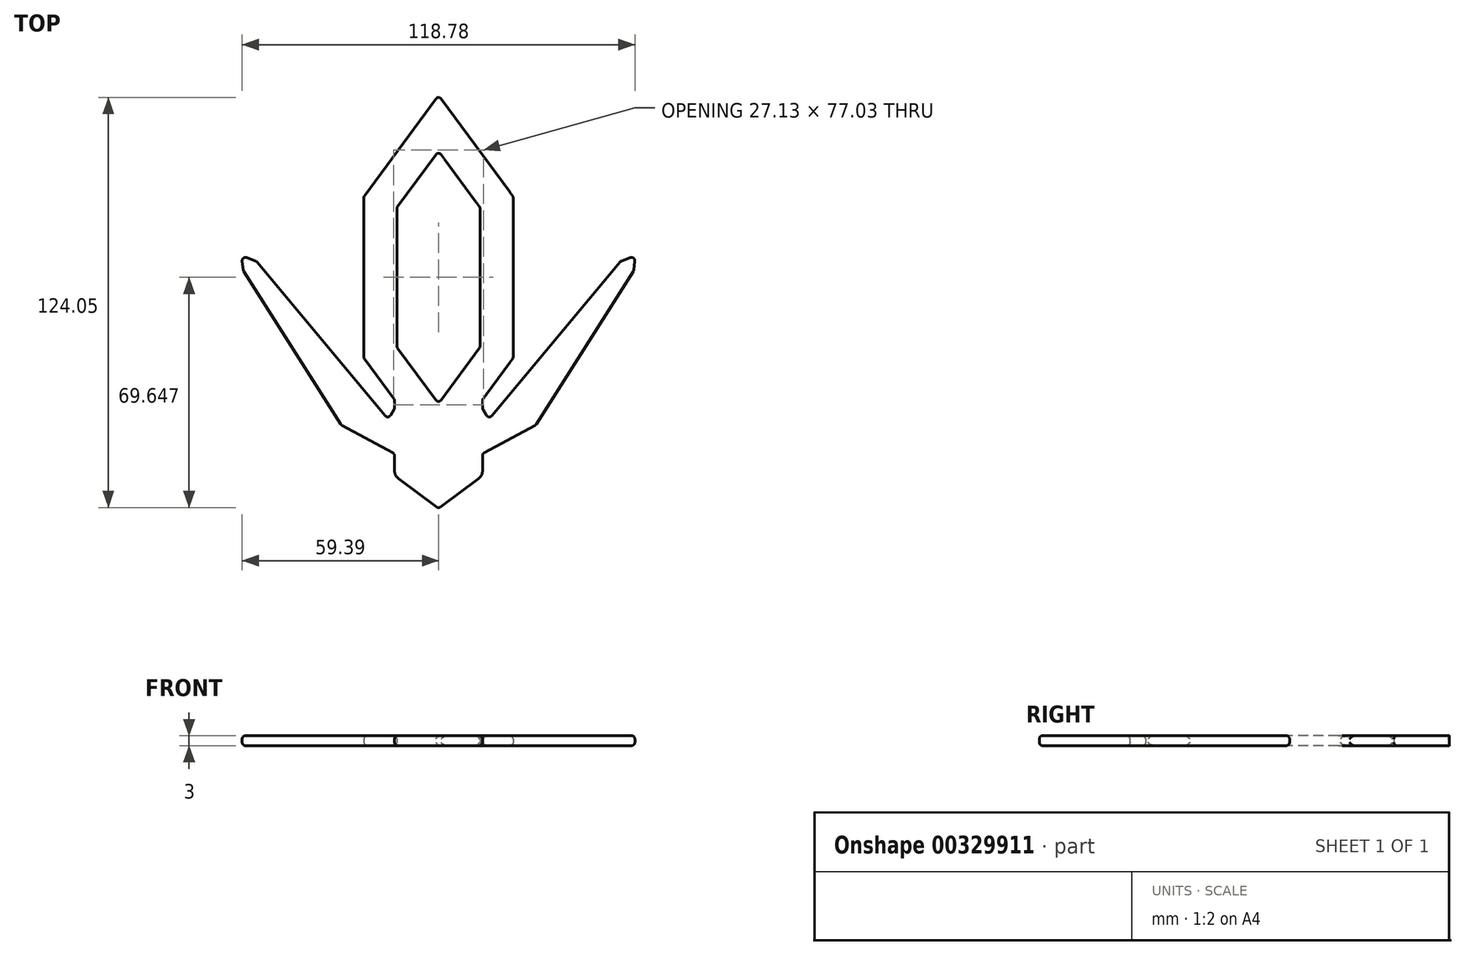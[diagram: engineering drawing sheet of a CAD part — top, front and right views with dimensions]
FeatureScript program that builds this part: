
annotation { "Feature Type Name" : "Feature", "Feature Type Description" : "" }
export const myFeature = defineFeature(function(context is Context, id is Id, definition is map)
    precondition{}
    {
        {
            var Q0;
            Q0=qCreatedBy(makeId("Top.planeOp"),FACE);
            var sketch = newSketch(context, id + "F0", { "sketchPlane" : qUnion([Q0])});
            skLineSegment(sketch, "E0", {"start": v(0, 55.08) * mm, "end": v(22.57, 24.43) * mm});
            skLineSegment(sketch, "E1", {"start": v(22.57, 24.43) * mm, "end": v(22.57, 0) * mm});
            skLineSegment(sketch, "E2.0", {"start": v(12.57, 21.15) * mm, "end": v(12.57, 0) * mm});
            skLineSegment(sketch, "E2.1", {"start": v(0, 38.21) * mm, "end": v(12.57, 21.15) * mm});
            skLineSegment(sketch, "E3.MirrorCS", {"start": v(-22.57, 24.43) * mm, "end": v(-22.57, 0) * mm});
            skLineSegment(sketch, "E4.MirrorCS", {"start": v(-12.57, 21.15) * mm, "end": v(-12.57, 0) * mm});
            skLineSegment(sketch, "E5.MirrorCS", {"start": v(0, 38.21) * mm, "end": v(-12.57, 21.15) * mm});
            skLineSegment(sketch, "E6.MirrorCS", {"start": v(0, 55.08) * mm, "end": v(-22.57, 24.43) * mm});
            skLineSegment(sketch, "E7.MirrorCS", {"start": v(-4.03, 49.61) * mm, "end": v(-22.57, 24.43) * mm});
            skLineSegment(sketch, "E8.MirrorCS", {"start": v(-22.57, 23.45) * mm, "end": v(-22.57, 0) * mm});
            skLineSegment(sketch, "E9.MirrorCS", {"start": v(12.57, 20.16) * mm, "end": v(12.57, 0) * mm});
            skLineSegment(sketch, "E10.MirrorCS", {"start": v(-12.57, 20.16) * mm, "end": v(-12.57, 0) * mm});
            skLineSegment(sketch, "E11.MirrorCS", {"start": v(-2.42, 34.93) * mm, "end": v(-11.98, 21.94) * mm});
            skLineSegment(sketch, "E12.MirrorCS", {"start": v(4.03, 49.61) * mm, "end": v(21.98, 25.23) * mm});
            skLineSegment(sketch, "E13.MirrorCS", {"start": v(0, 55.08) * mm, "end": v(-21.98, 25.23) * mm});
            skLineSegment(sketch, "E14.MirrorCS", {"start": v(22.57, 23.45) * mm, "end": v(22.57, 0) * mm});
            skLineSegment(sketch, "E15.MirrorCS", {"start": v(2.42, 34.93) * mm, "end": v(11.98, 21.94) * mm});
            skPoint(sketch, "E16.visualSharp", {"position": v(0, 55.08) * mm});
            skArc(sketch, "E16.filletArc", {"start": v(4.03, 49.61) * mm, "mid": v(0, 51.65) * mm, "end": v(-4.03, 49.61) * mm});
            skPoint(sketch, "E17.visualSharp", {"position": v(0, 38.21) * mm});
            skArc(sketch, "E17.filletArc", {"start": v(2.42, 34.93) * mm, "mid": v(0, 36.15) * mm, "end": v(-2.42, 34.93) * mm});
            skPoint(sketch, "E18.visualSharp", {"position": v(12.57, 21.15) * mm});
            skArc(sketch, "E18.filletArc", {"start": v(12.57, 20.16) * mm, "mid": v(12.42, 21.1) * mm, "end": v(11.98, 21.94) * mm});
            skPoint(sketch, "E19.visualSharp", {"position": v(-12.57, 21.15) * mm});
            skArc(sketch, "E19.filletArc", {"start": v(-11.98, 21.94) * mm, "mid": v(-12.42, 21.1) * mm, "end": v(-12.57, 20.16) * mm});
            skPoint(sketch, "E20.visualSharp", {"position": v(-22.57, 24.43) * mm});
            skArc(sketch, "E20.filletArc", {"start": v(-21.98, 25.23) * mm, "mid": v(-22.42, 24.39) * mm, "end": v(-22.57, 23.45) * mm});
            skPoint(sketch, "E21.visualSharp", {"position": v(22.57, 24.43) * mm});
            skArc(sketch, "E21.filletArc", {"start": v(22.57, 23.45) * mm, "mid": v(22.42, 24.39) * mm, "end": v(21.98, 25.23) * mm});
            skArc(sketch, "E22.MirrorCS", {"start": v(2.42, -34.93) * mm, "mid": v(0, -36.15) * mm, "end": v(-2.42, -34.93) * mm});
            skArc(sketch, "E23.MirrorCS", {"start": v(-11.98, -21.94) * mm, "mid": v(-12.42, -21.1) * mm, "end": v(-12.57, -20.16) * mm});
            skArc(sketch, "E24.MirrorCS", {"start": v(12.57, -20.16) * mm, "mid": v(12.42, -21.1) * mm, "end": v(11.98, -21.94) * mm});
            skArc(sketch, "E25.MirrorCS", {"start": v(-21.98, -25.23) * mm, "mid": v(-22.42, -24.39) * mm, "end": v(-22.57, -23.45) * mm});
            skArc(sketch, "E26.MirrorCS", {"start": v(22.57, -23.45) * mm, "mid": v(22.42, -24.39) * mm, "end": v(21.98, -25.23) * mm});
            skLineSegment(sketch, "E27.MirrorCS", {"start": v(12.57, -21.15) * mm, "end": v(12.57, 0) * mm});
            skLineSegment(sketch, "E28.MirrorCS", {"start": v(22.57, -24.43) * mm, "end": v(22.57, 0) * mm});
            skLineSegment(sketch, "E29.MirrorCS", {"start": v(-12.57, -21.15) * mm, "end": v(-12.57, 0) * mm});
            skLineSegment(sketch, "E30.MirrorCS", {"start": v(0, -38.21) * mm, "end": v(12.57, -21.15) * mm});
            skLineSegment(sketch, "E31.MirrorCS", {"start": v(-22.57, -24.43) * mm, "end": v(-22.57, 0) * mm});
            skLineSegment(sketch, "E32.MirrorCS", {"start": v(0, -38.21) * mm, "end": v(-12.57, -21.15) * mm});
            skLineSegment(sketch, "E33.MirrorCS", {"start": v(0, -55.08) * mm, "end": v(-22.57, -24.43) * mm});
            skLineSegment(sketch, "E34.MirrorCS", {"start": v(0, -55.08) * mm, "end": v(22.57, -24.43) * mm});
            skLineSegment(sketch, "E35.MirrorCS", {"start": v(-4.03, -49.61) * mm, "end": v(-22.57, -24.43) * mm});
            skPoint(sketch, "E36.MirrorP", {"position": v(0, -38.21) * mm});
            skLineSegment(sketch, "E37.MirrorCS", {"start": v(22.57, -23.45) * mm, "end": v(22.57, 0) * mm});
            skLineSegment(sketch, "E38.MirrorCS", {"start": v(4.03, -49.61) * mm, "end": v(21.98, -25.23) * mm});
            skLineSegment(sketch, "E39.MirrorCS", {"start": v(-2.42, -34.93) * mm, "end": v(-11.98, -21.94) * mm});
            skPoint(sketch, "E40.MirrorP", {"position": v(-22.57, -24.43) * mm});
            skPoint(sketch, "E41.MirrorP", {"position": v(22.57, -24.43) * mm});
            skLineSegment(sketch, "E42.MirrorCS", {"start": v(-22.57, -23.45) * mm, "end": v(-22.57, 0) * mm});
            skPoint(sketch, "E43.MirrorP", {"position": v(-12.57, -21.15) * mm});
            skPoint(sketch, "E44.MirrorP", {"position": v(12.57, -21.15) * mm});
            skLineSegment(sketch, "E45.MirrorCS", {"start": v(12.57, -20.16) * mm, "end": v(12.57, 0) * mm});
            skLineSegment(sketch, "E46.MirrorCS", {"start": v(0, -55.08) * mm, "end": v(-21.98, -25.23) * mm});
            skLineSegment(sketch, "E47.MirrorCS", {"start": v(-12.57, -20.16) * mm, "end": v(-12.57, 0) * mm});
            skLineSegment(sketch, "E48.MirrorCS", {"start": v(2.42, -34.93) * mm, "end": v(11.98, -21.94) * mm});
            skPoint(sketch, "E49.MirrorP", {"position": v(0, -55.08) * mm});
            skLineSegment(sketch, "E50", {"start": v(-13.3, -37.02) * mm, "end": v(-13.3, -58.54) * mm});
            skLineSegment(sketch, "E51", {"start": v(-12.08, -60.95) * mm, "end": v(0, -69.9) * mm});
            skPoint(sketch, "E52.visualSharp", {"position": v(-13.3, -60.05) * mm});
            skArc(sketch, "E52.filletArc", {"start": v(-13.3, -58.54) * mm, "mid": v(-12.98, -59.88) * mm, "end": v(-12.08, -60.95) * mm});
            skArc(sketch, "E53.MirrorCS", {"start": v(13.3, -58.54) * mm, "mid": v(12.98, -59.88) * mm, "end": v(12.08, -60.95) * mm});
            skLineSegment(sketch, "E54.MirrorCS", {"start": v(13.3, -37.02) * mm, "end": v(13.3, -58.54) * mm});
            skLineSegment(sketch, "E55.MirrorCS", {"start": v(12.08, -60.95) * mm, "end": v(0, -69.9) * mm});
            skPoint(sketch, "E56.MirrorP", {"position": v(13.3, -60.05) * mm});
            skPoint(sketch, "E57.endSnap0", {"position": v(-13.3, -47.78) * mm});
            skLineSegment(sketch, "E58", {"start": v(-13.3, -39.76) * mm, "end": v(-15.24, -42.93) * mm});
            skPoint(sketch, "E58.startSnap0", {"position": v(-11.28, -39.76) * mm});
            skLineSegment(sketch, "E59", {"start": v(-15.24, -42.93) * mm, "end": v(-55.04, 4.83) * mm});
            skLineSegment(sketch, "E60", {"start": v(-55.04, 4.83) * mm, "end": v(-59.6, 6.54) * mm});
            skLineSegment(sketch, "E61", {"start": v(-59.6, 6.54) * mm, "end": v(-59.02, 1.99) * mm});
            skLineSegment(sketch, "E62", {"start": v(-59.02, 1.99) * mm, "end": v(-29.45, -44.64) * mm});
            skLineSegment(sketch, "E63", {"start": v(-29.45, -44.64) * mm, "end": v(-13.3, -53.38) * mm});
            skLineSegment(sketch, "E64.MirrorCS", {"start": v(13.3, -39.76) * mm, "end": v(15.24, -42.93) * mm});
            skLineSegment(sketch, "E65.MirrorCS", {"start": v(29.45, -44.64) * mm, "end": v(13.3, -53.38) * mm});
            skLineSegment(sketch, "E66.MirrorCS", {"start": v(15.24, -42.93) * mm, "end": v(55.04, 4.83) * mm});
            skLineSegment(sketch, "E67.MirrorCS", {"start": v(55.04, 4.83) * mm, "end": v(59.6, 6.54) * mm});
            skLineSegment(sketch, "E68.MirrorCS", {"start": v(59.02, 1.99) * mm, "end": v(29.45, -44.64) * mm});
            skLineSegment(sketch, "E69.MirrorCS", {"start": v(59.6, 6.54) * mm, "end": v(59.02, 1.99) * mm});
            skSolve(sketch);
        }
        {
            var Q0;
            Q0 = qSketchRegion(id + "F0", true);
            extrude(context, id + "F1", {"entities" : qUnion([Q0]), "depth" : 3 * mm});
        }
        {
            var Q0;
            Q0=makeQuery(id+"F1.opExtrude","CAP_EDGE",EDGE,{"disambiguationData":[OSD([sQuery(id+"F0.wireOp",EDGE,"E33.MirrorCS"),sQuery(id+"F0.wireOp",EDGE,"E46.MirrorCS")])],"isStart":true});
            var Q1;
            Q1=makeQuery(id+"F1.opExtrude","CAP_EDGE",EDGE,{"disambiguationData":[OSD([sQuery(id+"F0.wireOp",EDGE,"E33.MirrorCS"),sQuery(id+"F0.wireOp",EDGE,"E46.MirrorCS")])],"isStart":false});
            var Q2;
            Q2=makeQuery(id+"F1.opExtrude","CAP_EDGE",EDGE,{"disambiguationData":[OSD([sQuery(id+"F0.wireOp",EDGE,"E4.MirrorCS"),sQuery(id+"F0.wireOp",EDGE,"E29.MirrorCS"),sQuery(id+"F0.wireOp",EDGE,"E47.MirrorCS")])],"isStart":false});
            var Q3;
            Q3=makeQuery(id+"F1.opExtrude","CAP_EDGE",EDGE,{"disambiguationData":[OSD([sQuery(id+"F0.wireOp",EDGE,"E3.MirrorCS"),sQuery(id+"F0.wireOp",EDGE,"E31.MirrorCS"),sQuery(id+"F0.wireOp",EDGE,"E42.MirrorCS")])],"isStart":true});
            var Q4;
            Q4=makeQuery(id+"F1.opExtrude","CAP_EDGE",EDGE,{"disambiguationData":[OSD([sQuery(id+"F0.wireOp",EDGE,"E3.MirrorCS"),sQuery(id+"F0.wireOp",EDGE,"E31.MirrorCS"),sQuery(id+"F0.wireOp",EDGE,"E42.MirrorCS")])],"isStart":false});
            var Q5;
            {var subQ0=sQuery(id+"F0.wireOp",EDGE,"E50");Q5=makeQuery(id+"F1.opExtrude","CAP_EDGE",EDGE,{"disambiguationData":[OSD([subQ0]),TDD([makeQuery(id+"F0.imprint","IMPRINT",EDGE,{"disambiguationData":[TD([[makeQuery(id+"F0.imprint","INTERSECT",VERTEX,{"derivedFrom":[sQuery(id+"F0.wireOp",EDGE,"E46.MirrorCS"),subQ0]}),-1.0]])],"derivedFrom":subQ0})])],"isStart":true});}
            var Q6;
            Q6=makeQuery(id+"F1.opExtrude","SWEPT_EDGE",EDGE,{"disambiguationData":[OSD([sQuery(id+"F0.wireOp",EDGE,"E32.MirrorCS"),sQuery(id+"F0.wireOp",EDGE,"E29.MirrorCS")])]});
            var Q7;
            {var subQ0=sQuery(id+"F0.wireOp",EDGE,"E50");Q7=makeQuery(id+"F1.opExtrude","CAP_EDGE",EDGE,{"disambiguationData":[OSD([subQ0]),TDD([makeQuery(id+"F0.imprint","IMPRINT",EDGE,{"disambiguationData":[TD([[makeQuery(id+"F0.imprint","INTERSECT",VERTEX,{"derivedFrom":[sQuery(id+"F0.wireOp",EDGE,"E46.MirrorCS"),subQ0]}),-1.0]])],"derivedFrom":subQ0})])],"isStart":false});}
            var Q8;
            Q8=makeQuery(id+"F1.opExtrude","CAP_EDGE",EDGE,{"disambiguationData":[OSD([sQuery(id+"F0.wireOp",EDGE,"E4.MirrorCS"),sQuery(id+"F0.wireOp",EDGE,"E29.MirrorCS"),sQuery(id+"F0.wireOp",EDGE,"E47.MirrorCS")])],"isStart":true});
            var Q9;
            Q9=makeQuery(id+"F1.opExtrude","SWEPT_EDGE",EDGE,{"disambiguationData":[OSD([sQuery(id+"F0.wireOp",EDGE,"E46.MirrorCS"),sQuery(id+"F0.wireOp",EDGE,"E50")])]});
            var Q10;
            Q10=makeQuery(id+"F1.opExtrude","SWEPT_EDGE",EDGE,{"disambiguationData":[OSD([sQuery(id+"F0.wireOp",EDGE,"E31.MirrorCS"),sQuery(id+"F0.wireOp",EDGE,"E33.MirrorCS")])]});
            var Q11;
            Q11=makeQuery(id+"F1.opExtrude","SWEPT_EDGE",EDGE,{"disambiguationData":[OSD([sQuery(id+"F0.wireOp",EDGE,"E3.MirrorCS"),sQuery(id+"F0.wireOp",EDGE,"E6.MirrorCS")])]});
            var Q12;
            Q12=makeQuery(id+"F1.opExtrude","SWEPT_EDGE",EDGE,{"disambiguationData":[OSD([sQuery(id+"F0.wireOp",EDGE,"E4.MirrorCS"),sQuery(id+"F0.wireOp",EDGE,"E5.MirrorCS")])]});
            var Q13;
            Q13=makeQuery(id+"F1.opExtrude","SWEPT_EDGE",EDGE,{"disambiguationData":[OSD([sQuery(id+"F0.wireOp",EDGE,"E50"),sQuery(id+"F0.wireOp",EDGE,"E52.filletArc")])]});
            var Q14;
            Q14=makeQuery(id+"F1.opExtrude","SWEPT_EDGE",EDGE,{"disambiguationData":[OSD([sQuery(id+"F0.wireOp",EDGE,"E50"),sQuery(id+"F0.wireOp",EDGE,"E58")])]});
            var Q15;
            Q15=makeQuery(id+"F1.opExtrude","SWEPT_EDGE",EDGE,{"disambiguationData":[OSD([sQuery(id+"F0.wireOp",EDGE,"E50"),sQuery(id+"F0.wireOp",EDGE,"E63")])]});
            var Q16;
            Q16=makeQuery(id+"F1.opExtrude","CAP_EDGE",EDGE,{"disambiguationData":[OSD([sQuery(id+"F0.wireOp",EDGE,"E30.MirrorCS"),sQuery(id+"F0.wireOp",EDGE,"E48.MirrorCS")])],"isStart":false});
            var Q17;
            Q17=makeQuery(id+"F1.opExtrude","CAP_EDGE",EDGE,{"disambiguationData":[OSD([sQuery(id+"F0.wireOp",EDGE,"E32.MirrorCS"),sQuery(id+"F0.wireOp",EDGE,"E39.MirrorCS")])],"isStart":false});
            var Q18;
            Q18=makeQuery(id+"F1.opExtrude","CAP_EDGE",EDGE,{"disambiguationData":[OSD([sQuery(id+"F0.wireOp",EDGE,"E2.1")])],"isStart":false});
            var Q19;
            Q19=makeQuery(id+"F1.opExtrude","CAP_EDGE",EDGE,{"disambiguationData":[OSD([sQuery(id+"F0.wireOp",EDGE,"E1"),sQuery(id+"F0.wireOp",EDGE,"E28.MirrorCS"),sQuery(id+"F0.wireOp",EDGE,"E37.MirrorCS")])],"isStart":false});
            var Q20;
            Q20=makeQuery(id+"F1.opExtrude","CAP_EDGE",EDGE,{"disambiguationData":[OSD([sQuery(id+"F0.wireOp",EDGE,"E32.MirrorCS"),sQuery(id+"F0.wireOp",EDGE,"E39.MirrorCS")])],"isStart":true});
            var Q21;
            Q21=makeQuery(id+"F1.opExtrude","CAP_EDGE",EDGE,{"disambiguationData":[OSD([sQuery(id+"F0.wireOp",EDGE,"E5.MirrorCS")])],"isStart":false});
            var Q22;
            Q22=makeQuery(id+"F1.opExtrude","CAP_EDGE",EDGE,{"disambiguationData":[OSD([sQuery(id+"F0.wireOp",EDGE,"E34.MirrorCS"),sQuery(id+"F0.wireOp",EDGE,"E38.MirrorCS")])],"isStart":false});
            var Q23;
            Q23=makeQuery(id+"F1.opExtrude","CAP_EDGE",EDGE,{"disambiguationData":[OSD([sQuery(id+"F0.wireOp",EDGE,"E0")])],"isStart":false});
            var Q24;
            Q24=makeQuery(id+"F1.opExtrude","CAP_EDGE",EDGE,{"disambiguationData":[OSD([sQuery(id+"F0.wireOp",EDGE,"E0")])],"isStart":true});
            var Q25;
            Q25=makeQuery(id+"F1.opExtrude","CAP_EDGE",EDGE,{"disambiguationData":[OSD([sQuery(id+"F0.wireOp",EDGE,"E5.MirrorCS")])],"isStart":true});
            var Q26;
            Q26=makeQuery(id+"F1.opExtrude","CAP_EDGE",EDGE,{"disambiguationData":[OSD([sQuery(id+"F0.wireOp",EDGE,"E6.MirrorCS")])],"isStart":false});
            var Q27;
            Q27=makeQuery(id+"F1.opExtrude","CAP_EDGE",EDGE,{"disambiguationData":[OSD([sQuery(id+"F0.wireOp",EDGE,"E55.MirrorCS")])],"isStart":false});
            var Q28;
            Q28=makeQuery(id+"F1.opExtrude","CAP_EDGE",EDGE,{"disambiguationData":[OSD([sQuery(id+"F0.wireOp",EDGE,"E55.MirrorCS")])],"isStart":true});
            var Q29;
            Q29=makeQuery(id+"F1.opExtrude","CAP_EDGE",EDGE,{"disambiguationData":[OSD([sQuery(id+"F0.wireOp",EDGE,"E52.filletArc")])],"isStart":false});
            var Q30;
            Q30=makeQuery(id+"F1.opExtrude","CAP_EDGE",EDGE,{"disambiguationData":[OSD([sQuery(id+"F0.wireOp",EDGE,"E2.0"),sQuery(id+"F0.wireOp",EDGE,"E27.MirrorCS"),sQuery(id+"F0.wireOp",EDGE,"E45.MirrorCS")])],"isStart":true});
            var Q31;
            Q31=makeQuery(id+"F1.opExtrude","CAP_EDGE",EDGE,{"disambiguationData":[OSD([sQuery(id+"F0.wireOp",EDGE,"E2.0"),sQuery(id+"F0.wireOp",EDGE,"E27.MirrorCS"),sQuery(id+"F0.wireOp",EDGE,"E45.MirrorCS")])],"isStart":false});
            var Q32;
            Q32=makeQuery(id+"F1.opExtrude","CAP_EDGE",EDGE,{"disambiguationData":[OSD([sQuery(id+"F0.wireOp",EDGE,"E1"),sQuery(id+"F0.wireOp",EDGE,"E28.MirrorCS"),sQuery(id+"F0.wireOp",EDGE,"E37.MirrorCS")])],"isStart":true});
            var Q33;
            Q33=makeQuery(id+"F1.opExtrude","SWEPT_EDGE",EDGE,{"disambiguationData":[OSD([sQuery(id+"F0.wireOp",EDGE,"E38.MirrorCS"),sQuery(id+"F0.wireOp",EDGE,"E54.MirrorCS")])]});
            var Q34;
            Q34=makeQuery(id+"F1.opExtrude","CAP_EDGE",EDGE,{"disambiguationData":[OSD([sQuery(id+"F0.wireOp",EDGE,"E34.MirrorCS"),sQuery(id+"F0.wireOp",EDGE,"E38.MirrorCS")])],"isStart":true});
            var Q35;
            Q35=makeQuery(id+"F1.opExtrude","CAP_EDGE",EDGE,{"disambiguationData":[OSD([sQuery(id+"F0.wireOp",EDGE,"E30.MirrorCS"),sQuery(id+"F0.wireOp",EDGE,"E48.MirrorCS")])],"isStart":true});
            var Q36;
            Q36=makeQuery(id+"F1.opExtrude","SWEPT_EDGE",EDGE,{"disambiguationData":[OSD([sQuery(id+"F0.wireOp",EDGE,"E30.MirrorCS"),sQuery(id+"F0.wireOp",EDGE,"E32.MirrorCS")])]});
            var Q37;
            Q37=makeQuery(id+"F1.opExtrude","CAP_EDGE",EDGE,{"disambiguationData":[OSD([sQuery(id+"F0.wireOp",EDGE,"E2.1")])],"isStart":true});
            var Q38;
            {var subQ0=sQuery(id+"F0.wireOp",EDGE,"E50");Q38=makeQuery(id+"F1.opExtrude","CAP_EDGE",EDGE,{"disambiguationData":[OSD([subQ0]),TDD([makeQuery(id+"F0.imprint","IMPRINT",EDGE,{"disambiguationData":[TD([[makeQuery(id+"F0.imprint","INTERSECT",VERTEX,{"derivedFrom":[subQ0,sQuery(id+"F0.wireOp",EDGE,"E52.filletArc")]}),1.0]])],"derivedFrom":subQ0})])],"isStart":true});}
            var Q39;
            {var subQ0=sQuery(id+"F0.wireOp",EDGE,"E54.MirrorCS");Q39=makeQuery(id+"F1.opExtrude","CAP_EDGE",EDGE,{"disambiguationData":[OSD([subQ0]),TDD([makeQuery(id+"F0.imprint","IMPRINT",EDGE,{"disambiguationData":[TD([[makeQuery(id+"F0.imprint","INTERSECT",VERTEX,{"derivedFrom":[sQuery(id+"F0.wireOp",EDGE,"E38.MirrorCS"),subQ0]}),-1.0]])],"derivedFrom":subQ0})])],"isStart":true});}
            var Q40;
            {var subQ0=sQuery(id+"F0.wireOp",EDGE,"E54.MirrorCS");Q40=makeQuery(id+"F1.opExtrude","CAP_EDGE",EDGE,{"disambiguationData":[OSD([subQ0]),TDD([makeQuery(id+"F0.imprint","IMPRINT",EDGE,{"disambiguationData":[TD([[makeQuery(id+"F0.imprint","INTERSECT",VERTEX,{"derivedFrom":[sQuery(id+"F0.wireOp",EDGE,"E53.MirrorCS"),subQ0]}),1.0]])],"derivedFrom":subQ0})])],"isStart":true});}
            var Q41;
            {var subQ0=sQuery(id+"F0.wireOp",EDGE,"E54.MirrorCS");Q41=makeQuery(id+"F1.opExtrude","CAP_EDGE",EDGE,{"disambiguationData":[OSD([subQ0]),TDD([makeQuery(id+"F0.imprint","IMPRINT",EDGE,{"disambiguationData":[TD([[makeQuery(id+"F0.imprint","INTERSECT",VERTEX,{"derivedFrom":[sQuery(id+"F0.wireOp",EDGE,"E38.MirrorCS"),subQ0]}),-1.0]])],"derivedFrom":subQ0})])],"isStart":false});}
            var Q42;
            {var subQ0=sQuery(id+"F0.wireOp",EDGE,"E54.MirrorCS");Q42=makeQuery(id+"F1.opExtrude","CAP_EDGE",EDGE,{"disambiguationData":[OSD([subQ0]),TDD([makeQuery(id+"F0.imprint","IMPRINT",EDGE,{"disambiguationData":[TD([[makeQuery(id+"F0.imprint","INTERSECT",VERTEX,{"derivedFrom":[sQuery(id+"F0.wireOp",EDGE,"E53.MirrorCS"),subQ0]}),1.0]])],"derivedFrom":subQ0})])],"isStart":false});}
            var Q43;
            Q43=makeQuery(id+"F1.opExtrude","CAP_EDGE",EDGE,{"disambiguationData":[OSD([sQuery(id+"F0.wireOp",EDGE,"E6.MirrorCS")])],"isStart":true});
            var Q44;
            Q44=makeQuery(id+"F1.opExtrude","CAP_EDGE",EDGE,{"disambiguationData":[OSD([sQuery(id+"F0.wireOp",EDGE,"E51")])],"isStart":true});
            var Q45;
            Q45=makeQuery(id+"F1.opExtrude","CAP_EDGE",EDGE,{"disambiguationData":[OSD([sQuery(id+"F0.wireOp",EDGE,"E53.MirrorCS")])],"isStart":false});
            var Q46;
            {var subQ0=sQuery(id+"F0.wireOp",EDGE,"E50");Q46=makeQuery(id+"F1.opExtrude","CAP_EDGE",EDGE,{"disambiguationData":[OSD([subQ0]),TDD([makeQuery(id+"F0.imprint","IMPRINT",EDGE,{"disambiguationData":[TD([[makeQuery(id+"F0.imprint","INTERSECT",VERTEX,{"derivedFrom":[subQ0,sQuery(id+"F0.wireOp",EDGE,"E52.filletArc")]}),1.0]])],"derivedFrom":subQ0})])],"isStart":false});}
            var Q47;
            Q47=makeQuery(id+"F1.opExtrude","CAP_EDGE",EDGE,{"disambiguationData":[OSD([sQuery(id+"F0.wireOp",EDGE,"E51")])],"isStart":false});
            var Q48;
            Q48=makeQuery(id+"F1.opExtrude","SWEPT_EDGE",EDGE,{"disambiguationData":[OSD([sQuery(id+"F0.wireOp",EDGE,"E27.MirrorCS"),sQuery(id+"F0.wireOp",EDGE,"E30.MirrorCS")])]});
            var Q49;
            Q49=makeQuery(id+"F1.opExtrude","SWEPT_EDGE",EDGE,{"disambiguationData":[OSD([sQuery(id+"F0.wireOp",EDGE,"E28.MirrorCS"),sQuery(id+"F0.wireOp",EDGE,"E34.MirrorCS")])]});
            var Q50;
            Q50=makeQuery(id+"F1.opExtrude","SWEPT_EDGE",EDGE,{"disambiguationData":[OSD([sQuery(id+"F0.wireOp",EDGE,"E2.1"),sQuery(id+"F0.wireOp",EDGE,"E2.0")])]});
            var Q51;
            Q51=makeQuery(id+"F1.opExtrude","SWEPT_EDGE",EDGE,{"disambiguationData":[OSD([sQuery(id+"F0.wireOp",EDGE,"E2.1"),sQuery(id+"F0.wireOp",EDGE,"E5.MirrorCS")])]});
            var Q52;
            Q52=makeQuery(id+"F1.opExtrude","SWEPT_EDGE",EDGE,{"disambiguationData":[OSD([sQuery(id+"F0.wireOp",EDGE,"E0"),sQuery(id+"F0.wireOp",EDGE,"E6.MirrorCS")])]});
            var Q53;
            Q53=makeQuery(id+"F1.opExtrude","SWEPT_EDGE",EDGE,{"disambiguationData":[OSD([sQuery(id+"F0.wireOp",EDGE,"E1"),sQuery(id+"F0.wireOp",EDGE,"E0")])]});
            var Q54;
            Q54=makeQuery(id+"F1.opExtrude","SWEPT_EDGE",EDGE,{"disambiguationData":[OSD([sQuery(id+"F0.wireOp",EDGE,"E51"),sQuery(id+"F0.wireOp",EDGE,"E55.MirrorCS")])]});
            var Q55;
            Q55=makeQuery(id+"F1.opExtrude","SWEPT_EDGE",EDGE,{"disambiguationData":[OSD([sQuery(id+"F0.wireOp",EDGE,"E51"),sQuery(id+"F0.wireOp",EDGE,"E52.filletArc")])]});
            var Q56;
            Q56=makeQuery(id+"F1.opExtrude","CAP_EDGE",EDGE,{"disambiguationData":[OSD([sQuery(id+"F0.wireOp",EDGE,"E52.filletArc")])],"isStart":true});
            var Q57;
            Q57=makeQuery(id+"F1.opExtrude","SWEPT_EDGE",EDGE,{"disambiguationData":[OSD([sQuery(id+"F0.wireOp",EDGE,"E53.MirrorCS"),sQuery(id+"F0.wireOp",EDGE,"E54.MirrorCS")])]});
            var Q58;
            Q58=makeQuery(id+"F1.opExtrude","SWEPT_EDGE",EDGE,{"disambiguationData":[OSD([sQuery(id+"F0.wireOp",EDGE,"E54.MirrorCS"),sQuery(id+"F0.wireOp",EDGE,"E64.MirrorCS")])]});
            var Q59;
            Q59=makeQuery(id+"F1.opExtrude","SWEPT_EDGE",EDGE,{"disambiguationData":[OSD([sQuery(id+"F0.wireOp",EDGE,"E54.MirrorCS"),sQuery(id+"F0.wireOp",EDGE,"E65.MirrorCS")])]});
            var Q60;
            Q60=makeQuery(id+"F1.opExtrude","SWEPT_EDGE",EDGE,{"disambiguationData":[OSD([sQuery(id+"F0.wireOp",EDGE,"E53.MirrorCS"),sQuery(id+"F0.wireOp",EDGE,"E55.MirrorCS")])]});
            var Q61;
            Q61=makeQuery(id+"F1.opExtrude","CAP_EDGE",EDGE,{"disambiguationData":[OSD([sQuery(id+"F0.wireOp",EDGE,"E53.MirrorCS")])],"isStart":true});
            var Q62;
            Q62=makeQuery(id+"F1.opExtrude","CAP_EDGE",EDGE,{"disambiguationData":[OSD([sQuery(id+"F0.wireOp",EDGE,"E59")])],"isStart":true});
            var Q63;
            Q63=makeQuery(id+"F1.opExtrude","CAP_EDGE",EDGE,{"disambiguationData":[OSD([sQuery(id+"F0.wireOp",EDGE,"E65.MirrorCS")])],"isStart":true});
            var Q64;
            Q64=makeQuery(id+"F1.opExtrude","CAP_EDGE",EDGE,{"disambiguationData":[OSD([sQuery(id+"F0.wireOp",EDGE,"E66.MirrorCS")])],"isStart":true});
            var Q65;
            Q65=makeQuery(id+"F1.opExtrude","CAP_EDGE",EDGE,{"disambiguationData":[OSD([sQuery(id+"F0.wireOp",EDGE,"E63")])],"isStart":true});
            var Q66;
            Q66=makeQuery(id+"F1.opExtrude","CAP_EDGE",EDGE,{"disambiguationData":[OSD([sQuery(id+"F0.wireOp",EDGE,"E67.MirrorCS")])],"isStart":true});
            var Q67;
            Q67=makeQuery(id+"F1.opExtrude","SWEPT_EDGE",EDGE,{"disambiguationData":[OSD([sQuery(id+"F0.wireOp",EDGE,"E67.MirrorCS"),sQuery(id+"F0.wireOp",EDGE,"E66.MirrorCS")])]});
            var Q68;
            Q68=makeQuery(id+"F1.opExtrude","CAP_EDGE",EDGE,{"disambiguationData":[OSD([sQuery(id+"F0.wireOp",EDGE,"E68.MirrorCS")])],"isStart":false});
            var Q69;
            Q69=makeQuery(id+"F1.opExtrude","CAP_EDGE",EDGE,{"disambiguationData":[OSD([sQuery(id+"F0.wireOp",EDGE,"E64.MirrorCS")])],"isStart":true});
            var Q70;
            Q70=makeQuery(id+"F1.opExtrude","CAP_EDGE",EDGE,{"disambiguationData":[OSD([sQuery(id+"F0.wireOp",EDGE,"E62")])],"isStart":true});
            var Q71;
            Q71=makeQuery(id+"F1.opExtrude","SWEPT_EDGE",EDGE,{"disambiguationData":[OSD([sQuery(id+"F0.wireOp",EDGE,"E65.MirrorCS"),sQuery(id+"F0.wireOp",EDGE,"E68.MirrorCS")])]});
            var Q72;
            Q72=makeQuery(id+"F1.opExtrude","CAP_EDGE",EDGE,{"disambiguationData":[OSD([sQuery(id+"F0.wireOp",EDGE,"E62")])],"isStart":false});
            var Q73;
            Q73=makeQuery(id+"F1.opExtrude","CAP_EDGE",EDGE,{"disambiguationData":[OSD([sQuery(id+"F0.wireOp",EDGE,"E59")])],"isStart":false});
            var Q74;
            Q74=makeQuery(id+"F1.opExtrude","CAP_EDGE",EDGE,{"disambiguationData":[OSD([sQuery(id+"F0.wireOp",EDGE,"E65.MirrorCS")])],"isStart":false});
            var Q75;
            Q75=makeQuery(id+"F1.opExtrude","CAP_EDGE",EDGE,{"disambiguationData":[OSD([sQuery(id+"F0.wireOp",EDGE,"E63")])],"isStart":false});
            var Q76;
            Q76=makeQuery(id+"F1.opExtrude","CAP_EDGE",EDGE,{"disambiguationData":[OSD([sQuery(id+"F0.wireOp",EDGE,"E68.MirrorCS")])],"isStart":true});
            var Q77;
            Q77=makeQuery(id+"F1.opExtrude","SWEPT_EDGE",EDGE,{"disambiguationData":[OSD([sQuery(id+"F0.wireOp",EDGE,"E67.MirrorCS"),sQuery(id+"F0.wireOp",EDGE,"E69.MirrorCS")])]});
            var Q78;
            Q78=makeQuery(id+"F1.opExtrude","CAP_EDGE",EDGE,{"disambiguationData":[OSD([sQuery(id+"F0.wireOp",EDGE,"E66.MirrorCS")])],"isStart":false});
            var Q79;
            Q79=makeQuery(id+"F1.opExtrude","CAP_EDGE",EDGE,{"disambiguationData":[OSD([sQuery(id+"F0.wireOp",EDGE,"E69.MirrorCS")])],"isStart":false});
            var Q80;
            Q80=makeQuery(id+"F1.opExtrude","CAP_EDGE",EDGE,{"disambiguationData":[OSD([sQuery(id+"F0.wireOp",EDGE,"E64.MirrorCS")])],"isStart":false});
            var Q81;
            Q81=makeQuery(id+"F1.opExtrude","SWEPT_EDGE",EDGE,{"disambiguationData":[OSD([sQuery(id+"F0.wireOp",EDGE,"E69.MirrorCS"),sQuery(id+"F0.wireOp",EDGE,"E68.MirrorCS")])]});
            var Q82;
            Q82=makeQuery(id+"F1.opExtrude","CAP_EDGE",EDGE,{"disambiguationData":[OSD([sQuery(id+"F0.wireOp",EDGE,"E67.MirrorCS")])],"isStart":false});
            var Q83;
            Q83=makeQuery(id+"F1.opExtrude","SWEPT_EDGE",EDGE,{"disambiguationData":[OSD([sQuery(id+"F0.wireOp",EDGE,"E64.MirrorCS"),sQuery(id+"F0.wireOp",EDGE,"E66.MirrorCS")])]});
            var Q84;
            Q84=makeQuery(id+"F1.opExtrude","SWEPT_EDGE",EDGE,{"disambiguationData":[OSD([sQuery(id+"F0.wireOp",EDGE,"E62"),sQuery(id+"F0.wireOp",EDGE,"E63")])]});
            var Q85;
            Q85=makeQuery(id+"F1.opExtrude","CAP_EDGE",EDGE,{"disambiguationData":[OSD([sQuery(id+"F0.wireOp",EDGE,"E69.MirrorCS")])],"isStart":true});
            var Q86;
            Q86=makeQuery(id+"F1.opExtrude","SWEPT_EDGE",EDGE,{"disambiguationData":[OSD([sQuery(id+"F0.wireOp",EDGE,"E58"),sQuery(id+"F0.wireOp",EDGE,"E59")])]});
            var Q87;
            Q87=makeQuery(id+"F1.opExtrude","CAP_EDGE",EDGE,{"disambiguationData":[OSD([sQuery(id+"F0.wireOp",EDGE,"E58")])],"isStart":true});
            var Q88;
            Q88=makeQuery(id+"F1.opExtrude","CAP_EDGE",EDGE,{"disambiguationData":[OSD([sQuery(id+"F0.wireOp",EDGE,"E58")])],"isStart":false});
            var Q89;
            Q89=makeQuery(id+"F1.opExtrude","SWEPT_EDGE",EDGE,{"disambiguationData":[OSD([sQuery(id+"F0.wireOp",EDGE,"E59"),sQuery(id+"F0.wireOp",EDGE,"E60")])]});
            var Q90;
            Q90=makeQuery(id+"F1.opExtrude","CAP_EDGE",EDGE,{"disambiguationData":[OSD([sQuery(id+"F0.wireOp",EDGE,"E60")])],"isStart":false});
            var Q91;
            Q91=makeQuery(id+"F1.opExtrude","CAP_EDGE",EDGE,{"disambiguationData":[OSD([sQuery(id+"F0.wireOp",EDGE,"E60")])],"isStart":true});
            var Q92;
            Q92=makeQuery(id+"F1.opExtrude","SWEPT_EDGE",EDGE,{"disambiguationData":[OSD([sQuery(id+"F0.wireOp",EDGE,"E60"),sQuery(id+"F0.wireOp",EDGE,"E61")])]});
            var Q93;
            Q93=makeQuery(id+"F1.opExtrude","CAP_EDGE",EDGE,{"disambiguationData":[OSD([sQuery(id+"F0.wireOp",EDGE,"E61")])],"isStart":true});
            var Q94;
            Q94=makeQuery(id+"F1.opExtrude","SWEPT_EDGE",EDGE,{"disambiguationData":[OSD([sQuery(id+"F0.wireOp",EDGE,"E61"),sQuery(id+"F0.wireOp",EDGE,"E62")])]});
            var Q95;
            Q95=makeQuery(id+"F1.opExtrude","CAP_EDGE",EDGE,{"disambiguationData":[OSD([sQuery(id+"F0.wireOp",EDGE,"E61")])],"isStart":false});
            fillet(context, id + "F2", {"entities" : qUnion([Q0, Q1, Q2, Q3, Q4, Q5, Q6, Q7, Q8, Q9, Q10, Q11, Q12, Q13, Q14, Q15, Q16, Q17, Q18, Q19, Q20, Q21, Q22, Q23, Q24, Q25, Q26, Q27, Q28, Q29, Q30, Q31, Q32, Q33, Q34, Q35, Q36, Q37, Q38, Q39, Q40, Q41, Q42, Q43, Q44, Q45, Q46, Q47, Q48, Q49, Q50, Q51, Q52, Q53, Q54, Q55, Q56, Q57, Q58, Q59, Q60, Q61, Q62, Q63, Q64, Q65, Q66, Q67, Q68, Q69, Q70, Q71, Q72, Q73, Q74, Q75, Q76, Q77, Q78, Q79, Q80, Q81, Q82, Q83, Q84, Q85, Q86, Q87, Q88, Q89, Q90, Q91, Q92, Q93, Q94, Q95]), "radius" : 1 * mm, "tangentPropagation" : true, "allowEdgeOverflow" : false});
        }
    });
